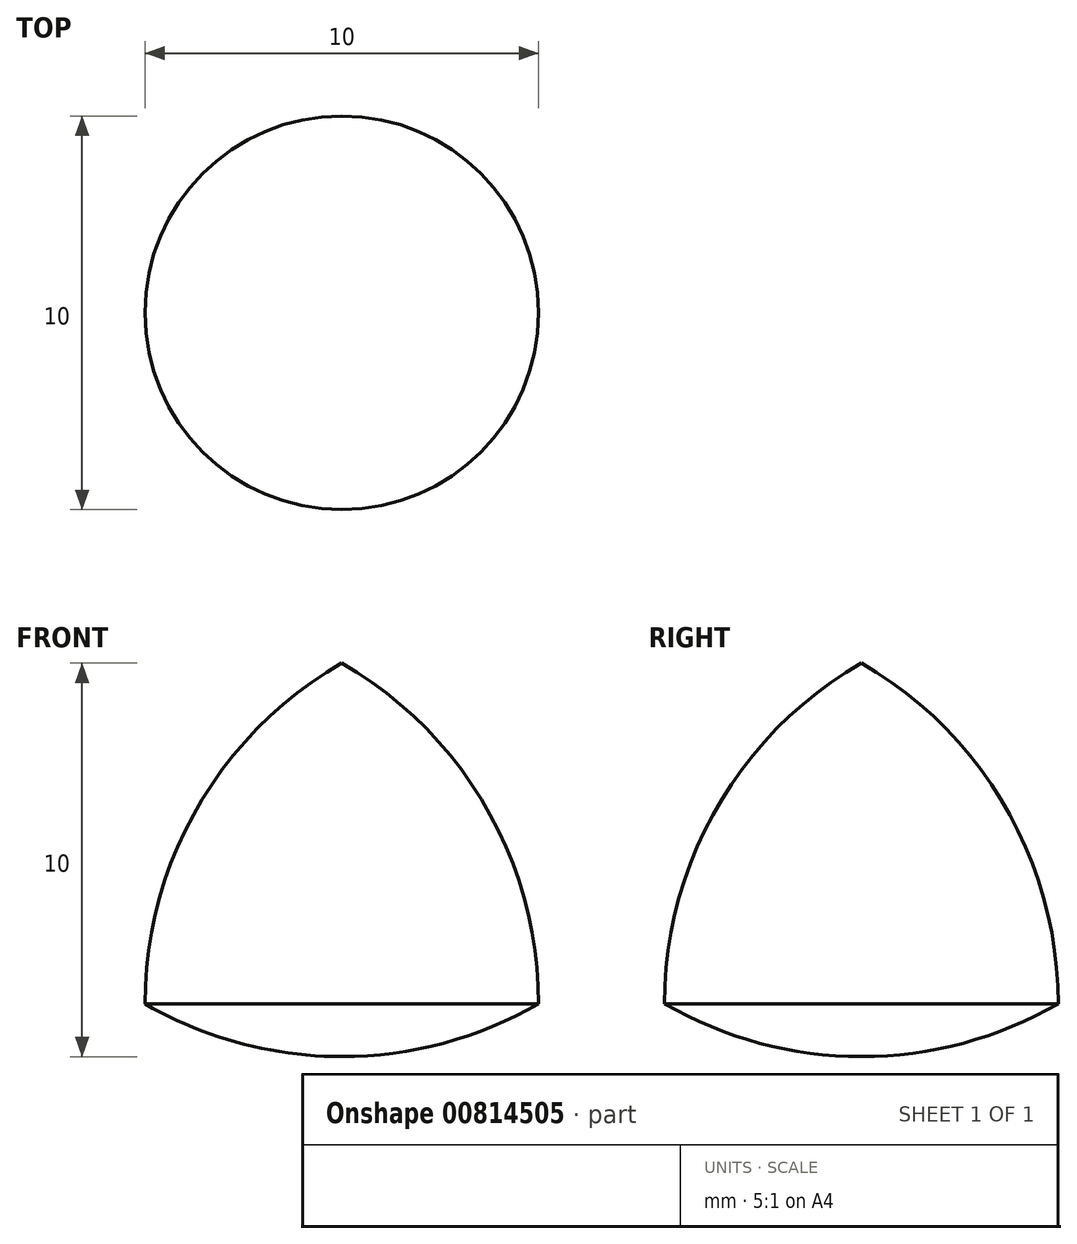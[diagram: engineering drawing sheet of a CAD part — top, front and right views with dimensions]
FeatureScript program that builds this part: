
annotation { "Feature Type Name" : "Feature", "Feature Type Description" : "" }
export const myFeature = defineFeature(function(context is Context, id is Id, definition is map)
    precondition{}
    {
        {
            var Q0;
            Q0=qCreatedBy(makeId("Front.planeOp"),FACE);
            var sketch = newSketch(context, id + "F0", { "sketchPlane" : qUnion([Q0])});
            skArc(sketch, "E0.cCircle", {"start": v(0, -2.89) * mm, "mid": v(2.89, 0) * mm, "end": v(0, 2.89) * mm, "construction": true});
            skLineSegment(sketch, "E0.0", {"start": v(5, -2.89) * mm, "end": v(0, -2.89) * mm});
            skLineSegment(sketch, "E0.2", {"start": v(0, 5.77) * mm, "end": v(5, -2.89) * mm});
            skPoint(sketch, "E0.0.midPoint", {"position": v(0, -2.89) * mm});
            skArc(sketch, "E1", {"start": v(5, -2.89) * mm, "mid": v(3.66, 2.11) * mm, "end": v(0, 5.77) * mm});
            skArc(sketch, "E2", {"start": v(0, -4.23) * mm, "mid": v(2.59, -3.89) * mm, "end": v(5, -2.89) * mm});
            skLineSegment(sketch, "E3", {"start": v(0, 22.94) * mm, "end": v(0, -20.44) * mm});
            skSolve(sketch);
        }
        {
            var Q0;
            {var subQ0=sQuery(id+"F0.wireOp",EDGE,"E2");var subQ3=sQuery(id+"F0.wireOp",EDGE,"E3");var subQ5=makeQuery(id+"F0.imprint","INTERSECT",VERTEX,{"derivedFrom":[subQ0,subQ3]});Q0=makeQuery(id+"F0.imprint","IMPRINT",FACE,{"disambiguationData":[TD([[makeQuery(id+"F0.imprint","IMPRINT",EDGE,{"disambiguationData":[TD([[subQ5,1.0]])],"derivedFrom":subQ3}),-1.0]])]});}
            var Q1;
            {var subQ1=sQuery(id+"F0.wireOp",EDGE,"E0.2");Q1=makeQuery(id+"F0.imprint","IMPRINT",FACE,{"disambiguationData":[TD([[makeQuery(id+"F0.imprint","IMPRINT",EDGE,{"derivedFrom":subQ1}),-1.0]])]});}
            var Q2;
            Q2=makeQuery(id+"F0.imprint","IMPRINT",FACE,{"disambiguationData":[TD([[makeQuery(id+"F0.imprint","IMPRINT",EDGE,{"derivedFrom":sQuery(id+"F0.wireOp",EDGE,"E0.2")}),1.0]])]});
            var Q3;
            {var subQ0=sQuery(id+"F0.wireOp",EDGE,"E0.0");Q3=makeQuery(id+"F0.imprint","IMPRINT",FACE,{"disambiguationData":[TD([[makeQuery(id+"F0.imprint","IMPRINT",EDGE,{"derivedFrom":subQ0}),1.0]])]});}
            var Q4;
            Q4=sQuery(id+"F0.wireOp",EDGE,"E3");
            revolve(context, id + "F1", {"surfaceOperationType" : NewSurfaceOperationType.NEW, "entities" : qUnion([Q0, Q1, Q2, Q3]), "axis" : qUnion([Q4]), "revolveType" : RevolveType.FULL});
        }
    });
